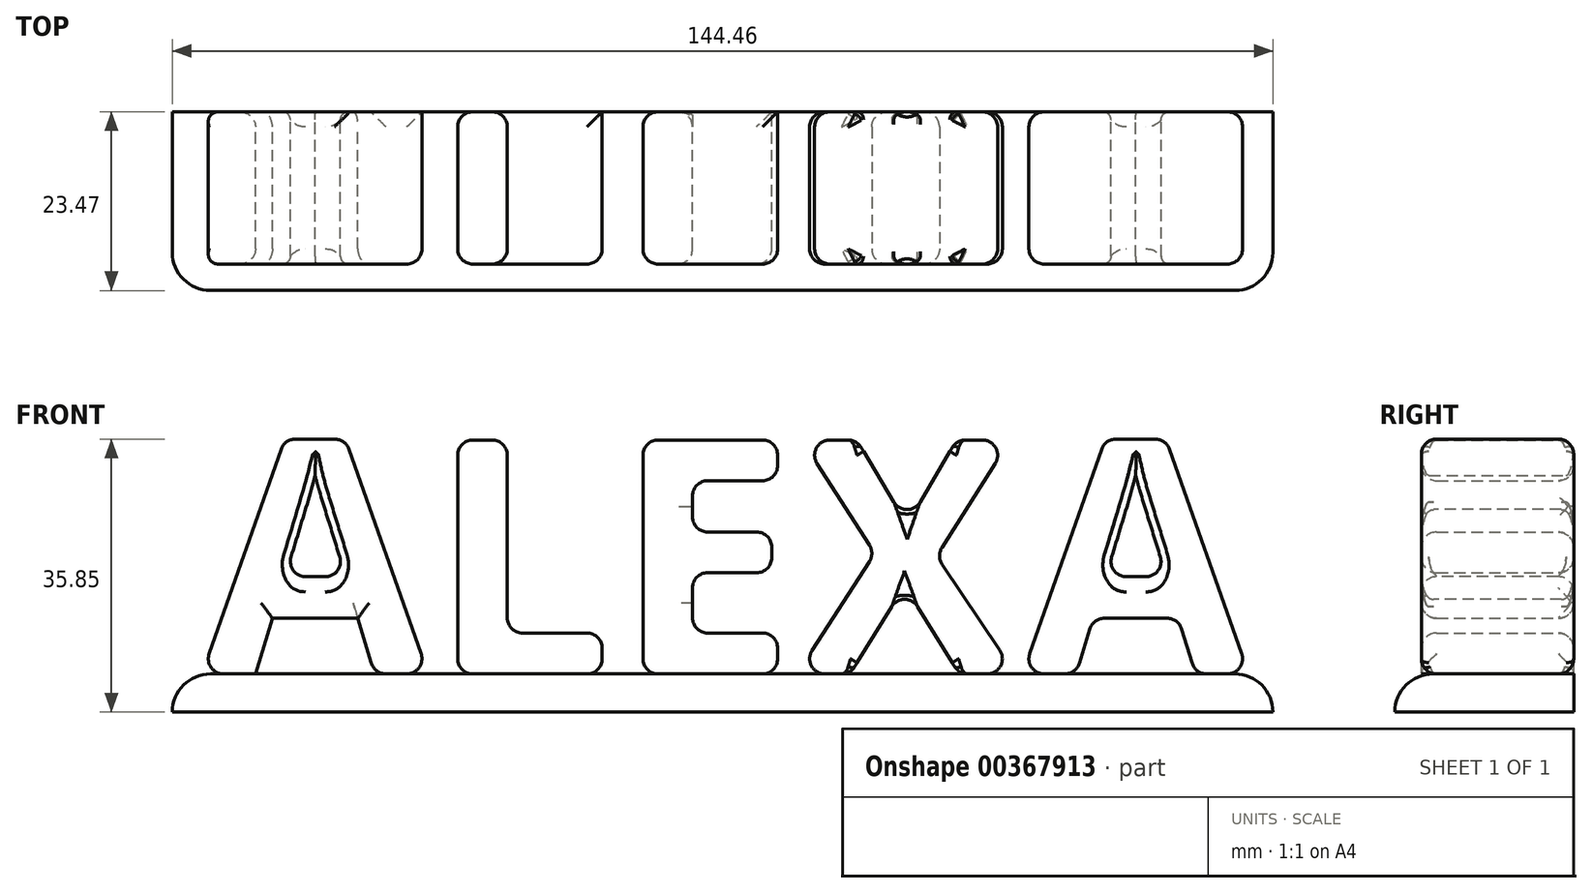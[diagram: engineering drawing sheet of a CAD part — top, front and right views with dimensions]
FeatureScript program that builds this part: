
annotation { "Feature Type Name" : "Feature", "Feature Type Description" : "" }
export const myFeature = defineFeature(function(context is Context, id is Id, definition is map)
    precondition{}
    {
        {
            var Q0;
            Q0=qCreatedBy(makeId("Front.planeOp"),FACE);
            var sketch = newSketch(context, id + "F0", { "sketchPlane" : qUnion([Q0])});
            skText(sketch, "E0", { "text": "ALEXA", "fontName": "OpenSans-Bold.ttf"});
            const initialGuessF0  = {"E0": [-0.06964, 0, 1, 0, 0.03098]};
            skSetInitialGuess(sketch, initialGuessF0);
            skSolve(sketch);
        }
        {
            var Q0;
            Q0 = qSketchRegion(id + "F0", true);
            extrude(context, id + "F1", {"entities" : qUnion([Q0]), "depth" : 20 * mm});
        }
        {
            var Q0;
            Q0=makeQuery(id+"F1.opExtrude","CAP_EDGE",EDGE,{"disambiguationData":[OSD([sQuery(id+"F0.wireOp",EDGE,"E0.sketch_text.stroke-8")])],"isStart":false});
            var Q1;
            Q1=makeQuery(id+"F1.opExtrude","CAP_EDGE",EDGE,{"disambiguationData":[OSD([sQuery(id+"F0.wireOp",EDGE,"E0.sketch_text.stroke-10")])],"isStart":false});
            var Q2;
            Q2=makeQuery(id+"F1.opExtrude","CAP_EDGE",EDGE,{"disambiguationData":[OSD([sQuery(id+"F0.wireOp",EDGE,"E0.sketch_text.stroke-37")])],"isStart":false});
            var Q3;
            Q3=makeQuery(id+"F1.opExtrude","CAP_EDGE",EDGE,{"disambiguationData":[OSD([sQuery(id+"F0.wireOp",EDGE,"E0.sketch_text.stroke-38")])],"isStart":false});
            var Q4;
            Q4=makeQuery(id+"F1.opExtrude","CAP_EDGE",EDGE,{"disambiguationData":[OSD([sQuery(id+"F0.wireOp",EDGE,"E0.sketch_text.stroke-31")])],"isStart":false});
            var Q5;
            Q5=makeQuery(id+"F1.opExtrude","CAP_EDGE",EDGE,{"disambiguationData":[OSD([sQuery(id+"F0.wireOp",EDGE,"E0.sketch_text.stroke-32")])],"isStart":false});
            var Q6;
            Q6=makeQuery(id+"F1.opExtrude","CAP_EDGE",EDGE,{"disambiguationData":[OSD([sQuery(id+"F0.wireOp",EDGE,"E0.sketch_text.stroke-50")])],"isStart":false});
            var Q7;
            Q7=makeQuery(id+"F1.opExtrude","CAP_EDGE",EDGE,{"disambiguationData":[OSD([sQuery(id+"F0.wireOp",EDGE,"E0.sketch_text.stroke-52")])],"isStart":false});
            var Q8;
            Q8=makeQuery(id+"F1.opExtrude","CAP_EDGE",EDGE,{"disambiguationData":[OSD([sQuery(id+"F0.wireOp",EDGE,"E0.sketch_text.stroke-52")])],"isStart":true});
            var Q9;
            Q9=makeQuery(id+"F1.opExtrude","CAP_EDGE",EDGE,{"disambiguationData":[OSD([sQuery(id+"F0.wireOp",EDGE,"E0.sketch_text.stroke-50")])],"isStart":true});
            var Q10;
            Q10=makeQuery(id+"F1.opExtrude","CAP_EDGE",EDGE,{"disambiguationData":[OSD([sQuery(id+"F0.wireOp",EDGE,"E0.sketch_text.stroke-38")])],"isStart":true});
            var Q11;
            Q11=makeQuery(id+"F1.opExtrude","CAP_EDGE",EDGE,{"disambiguationData":[OSD([sQuery(id+"F0.wireOp",EDGE,"E0.sketch_text.stroke-37")])],"isStart":true});
            var Q12;
            Q12=makeQuery(id+"F1.opExtrude","CAP_EDGE",EDGE,{"disambiguationData":[OSD([sQuery(id+"F0.wireOp",EDGE,"E0.sketch_text.stroke-32")])],"isStart":true});
            var Q13;
            Q13=makeQuery(id+"F1.opExtrude","CAP_EDGE",EDGE,{"disambiguationData":[OSD([sQuery(id+"F0.wireOp",EDGE,"E0.sketch_text.stroke-31")])],"isStart":true});
            var Q14;
            Q14=makeQuery(id+"F1.opExtrude","CAP_EDGE",EDGE,{"disambiguationData":[OSD([sQuery(id+"F0.wireOp",EDGE,"E0.sketch_text.stroke-8")])],"isStart":true});
            var Q15;
            Q15=makeQuery(id+"F1.opExtrude","CAP_EDGE",EDGE,{"disambiguationData":[OSD([sQuery(id+"F0.wireOp",EDGE,"E0.sketch_text.stroke-10")])],"isStart":true});
            fillet(context, id + "F2", {"entities" : qUnion([Q0, Q1, Q2, Q3, Q4, Q5, Q6, Q7, Q8, Q9, Q10, Q11, Q12, Q13, Q14, Q15]), "radius" : 1 * mm, "tangentPropagation" : true, "allowEdgeOverflow" : false});
        }
        {
            var Q0;
            Q0=makeQuery(id+"F1.opExtrude","CAP_EDGE",EDGE,{"disambiguationData":[OSD([sQuery(id+"F0.wireOp",EDGE,"E0.sketch_text.stroke-5")])],"isStart":false});
            var Q1;
            Q1=makeQuery(id+"F1.opExtrude","CAP_EDGE",EDGE,{"disambiguationData":[OSD([sQuery(id+"F0.wireOp",EDGE,"E0.sketch_text.stroke-4")])],"isStart":false});
            var Q2;
            Q2=makeQuery(id+"F1.opExtrude","CAP_EDGE",EDGE,{"disambiguationData":[OSD([sQuery(id+"F0.wireOp",EDGE,"E0.sketch_text.stroke-6")])],"isStart":false});
            var Q3;
            Q3=makeQuery(id+"F1.opExtrude","CAP_EDGE",EDGE,{"disambiguationData":[OSD([sQuery(id+"F0.wireOp",EDGE,"E0.sketch_text.stroke-11")])],"isStart":false});
            var Q4;
            Q4=makeQuery(id+"F1.opExtrude","CAP_EDGE",EDGE,{"disambiguationData":[OSD([sQuery(id+"F0.wireOp",EDGE,"E0.sketch_text.stroke-0")])],"isStart":false});
            var Q5;
            Q5=makeQuery(id+"F1.opExtrude","CAP_EDGE",EDGE,{"disambiguationData":[OSD([sQuery(id+"F0.wireOp",EDGE,"E0.sketch_text.stroke-2")])],"isStart":false});
            var Q6;
            Q6=makeQuery(id+"F1.opExtrude","CAP_EDGE",EDGE,{"disambiguationData":[OSD([sQuery(id+"F0.wireOp",EDGE,"E0.sketch_text.stroke-1")])],"isStart":false});
            var Q7;
            Q7=makeQuery(id+"F1.opExtrude","CAP_EDGE",EDGE,{"disambiguationData":[OSD([sQuery(id+"F0.wireOp",EDGE,"E0.sketch_text.stroke-7")])],"isStart":false});
            var Q8;
            Q8=makeQuery(id+"F1.opExtrude","SWEPT_EDGE",EDGE,{"disambiguationData":[OSD([sQuery(id+"F0.wireOp",EDGE,"E0.sketch_text.stroke-0"),sQuery(id+"F0.wireOp",EDGE,"E0.sketch_text.stroke-7")])]});
            var Q9;
            Q9=makeQuery(id+"F1.opExtrude","CAP_EDGE",EDGE,{"disambiguationData":[OSD([sQuery(id+"F0.wireOp",EDGE,"E0.sketch_text.stroke-7")])],"isStart":true});
            var Q10;
            Q10=makeQuery(id+"F1.opExtrude","SWEPT_EDGE",EDGE,{"disambiguationData":[OSD([sQuery(id+"F0.wireOp",EDGE,"E0.sketch_text.stroke-6"),sQuery(id+"F0.wireOp",EDGE,"E0.sketch_text.stroke-7")])]});
            var Q11;
            Q11=makeQuery(id+"F1.opExtrude","SWEPT_EDGE",EDGE,{"disambiguationData":[OSD([sQuery(id+"F0.wireOp",EDGE,"E0.sketch_text.stroke-5"),sQuery(id+"F0.wireOp",EDGE,"E0.sketch_text.stroke-6")])]});
            var Q12;
            Q12=makeQuery(id+"F1.opExtrude","SWEPT_EDGE",EDGE,{"disambiguationData":[OSD([sQuery(id+"F0.wireOp",EDGE,"E0.sketch_text.stroke-4"),sQuery(id+"F0.wireOp",EDGE,"E0.sketch_text.stroke-5")])]});
            var Q13;
            Q13=makeQuery(id+"F1.opExtrude","CAP_EDGE",EDGE,{"disambiguationData":[OSD([sQuery(id+"F0.wireOp",EDGE,"E0.sketch_text.stroke-4")])],"isStart":true});
            var Q14;
            Q14=makeQuery(id+"F1.opExtrude","SWEPT_EDGE",EDGE,{"disambiguationData":[OSD([sQuery(id+"F0.wireOp",EDGE,"E0.sketch_text.stroke-3"),sQuery(id+"F0.wireOp",EDGE,"E0.sketch_text.stroke-4")])]});
            var Q15;
            Q15=makeQuery(id+"F1.opExtrude","CAP_EDGE",EDGE,{"disambiguationData":[OSD([sQuery(id+"F0.wireOp",EDGE,"E0.sketch_text.stroke-2")])],"isStart":true});
            var Q16;
            Q16=makeQuery(id+"F1.opExtrude","CAP_EDGE",EDGE,{"disambiguationData":[OSD([sQuery(id+"F0.wireOp",EDGE,"E0.sketch_text.stroke-1")])],"isStart":true});
            var Q17;
            Q17=makeQuery(id+"F1.opExtrude","CAP_EDGE",EDGE,{"disambiguationData":[OSD([sQuery(id+"F0.wireOp",EDGE,"E0.sketch_text.stroke-5")])],"isStart":true});
            var Q18;
            Q18=makeQuery(id+"F1.opExtrude","SWEPT_FACE",FACE,{"disambiguationData":[OSD([sQuery(id+"F0.wireOp",EDGE,"E0.sketch_text.stroke-13")])]});
            var Q19;
            Q19=makeQuery(id+"F1.opExtrude","SWEPT_FACE",FACE,{"disambiguationData":[OSD([sQuery(id+"F0.wireOp",EDGE,"E0.sketch_text.stroke-12")])]});
            var Q20;
            Q20=makeQuery(id+"F1.opExtrude","SWEPT_FACE",FACE,{"disambiguationData":[OSD([sQuery(id+"F0.wireOp",EDGE,"E0.sketch_text.stroke-15")])]});
            var Q21;
            Q21=makeQuery(id+"F1.opExtrude","SWEPT_FACE",FACE,{"disambiguationData":[OSD([sQuery(id+"F0.wireOp",EDGE,"E0.sketch_text.stroke-14")])]});
            var Q22;
            Q22=makeQuery(id+"F1.opExtrude","CAP_FACE",FACE,{"disambiguationData":[OSD([sQuery(id+"F0.wireOp",EDGE,"E0.sketch_text.stroke-12"),sQuery(id+"F0.wireOp",EDGE,"E0.sketch_text.stroke-13"),sQuery(id+"F0.wireOp",EDGE,"E0.sketch_text.stroke-14"),sQuery(id+"F0.wireOp",EDGE,"E0.sketch_text.stroke-15"),sQuery(id+"F0.wireOp",EDGE,"E0.sketch_text.stroke-16"),sQuery(id+"F0.wireOp",EDGE,"E0.sketch_text.stroke-17")])],"isStart":false});
            var Q23;
            Q23=makeQuery(id+"F1.opExtrude","CAP_FACE",FACE,{"disambiguationData":[OSD([sQuery(id+"F0.wireOp",EDGE,"E0.sketch_text.stroke-18"),sQuery(id+"F0.wireOp",EDGE,"E0.sketch_text.stroke-19"),sQuery(id+"F0.wireOp",EDGE,"E0.sketch_text.stroke-20"),sQuery(id+"F0.wireOp",EDGE,"E0.sketch_text.stroke-21"),sQuery(id+"F0.wireOp",EDGE,"E0.sketch_text.stroke-22"),sQuery(id+"F0.wireOp",EDGE,"E0.sketch_text.stroke-23"),sQuery(id+"F0.wireOp",EDGE,"E0.sketch_text.stroke-24"),sQuery(id+"F0.wireOp",EDGE,"E0.sketch_text.stroke-25"),sQuery(id+"F0.wireOp",EDGE,"E0.sketch_text.stroke-26"),sQuery(id+"F0.wireOp",EDGE,"E0.sketch_text.stroke-27"),sQuery(id+"F0.wireOp",EDGE,"E0.sketch_text.stroke-28"),sQuery(id+"F0.wireOp",EDGE,"E0.sketch_text.stroke-29")])],"isStart":false});
            var Q24;
            Q24=makeQuery(id+"F1.opExtrude","SWEPT_FACE",FACE,{"disambiguationData":[OSD([sQuery(id+"F0.wireOp",EDGE,"E0.sketch_text.stroke-20")])]});
            var Q25;
            Q25=makeQuery(id+"F1.opExtrude","SWEPT_FACE",FACE,{"disambiguationData":[OSD([sQuery(id+"F0.wireOp",EDGE,"E0.sketch_text.stroke-19")])]});
            var Q26;
            Q26=makeQuery(id+"F1.opExtrude","SWEPT_FACE",FACE,{"disambiguationData":[OSD([sQuery(id+"F0.wireOp",EDGE,"E0.sketch_text.stroke-22")])]});
            var Q27;
            Q27=makeQuery(id+"F1.opExtrude","SWEPT_FACE",FACE,{"disambiguationData":[OSD([sQuery(id+"F0.wireOp",EDGE,"E0.sketch_text.stroke-26")])]});
            var Q28;
            Q28=makeQuery(id+"F1.opExtrude","SWEPT_FACE",FACE,{"disambiguationData":[OSD([sQuery(id+"F0.wireOp",EDGE,"E0.sketch_text.stroke-18")])]});
            var Q29;
            Q29=makeQuery(id+"F1.opExtrude","SWEPT_FACE",FACE,{"disambiguationData":[OSD([sQuery(id+"F0.wireOp",EDGE,"E0.sketch_text.stroke-28")])]});
            var Q30;
            Q30=makeQuery(id+"F1.opExtrude","SWEPT_FACE",FACE,{"disambiguationData":[OSD([sQuery(id+"F0.wireOp",EDGE,"E0.sketch_text.stroke-24")])]});
            var Q31;
            Q31=makeQuery(id+"F1.opExtrude","CAP_FACE",FACE,{"disambiguationData":[OSD([sQuery(id+"F0.wireOp",EDGE,"E0.sketch_text.stroke-30"),sQuery(id+"F0.wireOp",EDGE,"E0.sketch_text.stroke-31"),sQuery(id+"F0.wireOp",EDGE,"E0.sketch_text.stroke-32"),sQuery(id+"F0.wireOp",EDGE,"E0.sketch_text.stroke-33"),sQuery(id+"F0.wireOp",EDGE,"E0.sketch_text.stroke-34"),sQuery(id+"F0.wireOp",EDGE,"E0.sketch_text.stroke-35"),sQuery(id+"F0.wireOp",EDGE,"E0.sketch_text.stroke-36"),sQuery(id+"F0.wireOp",EDGE,"E0.sketch_text.stroke-37"),sQuery(id+"F0.wireOp",EDGE,"E0.sketch_text.stroke-38"),sQuery(id+"F0.wireOp",EDGE,"E0.sketch_text.stroke-39"),sQuery(id+"F0.wireOp",EDGE,"E0.sketch_text.stroke-40"),sQuery(id+"F0.wireOp",EDGE,"E0.sketch_text.stroke-41")])],"isStart":false});
            var Q32;
            Q32=makeQuery(id+"F1.opExtrude","CAP_FACE",FACE,{"disambiguationData":[OSD([sQuery(id+"F0.wireOp",EDGE,"E0.sketch_text.stroke-30"),sQuery(id+"F0.wireOp",EDGE,"E0.sketch_text.stroke-31"),sQuery(id+"F0.wireOp",EDGE,"E0.sketch_text.stroke-32"),sQuery(id+"F0.wireOp",EDGE,"E0.sketch_text.stroke-33"),sQuery(id+"F0.wireOp",EDGE,"E0.sketch_text.stroke-34"),sQuery(id+"F0.wireOp",EDGE,"E0.sketch_text.stroke-35"),sQuery(id+"F0.wireOp",EDGE,"E0.sketch_text.stroke-36"),sQuery(id+"F0.wireOp",EDGE,"E0.sketch_text.stroke-37"),sQuery(id+"F0.wireOp",EDGE,"E0.sketch_text.stroke-38"),sQuery(id+"F0.wireOp",EDGE,"E0.sketch_text.stroke-39"),sQuery(id+"F0.wireOp",EDGE,"E0.sketch_text.stroke-40"),sQuery(id+"F0.wireOp",EDGE,"E0.sketch_text.stroke-41")])],"isStart":true});
            var Q33;
            Q33=makeQuery(id+"F1.opExtrude","SWEPT_FACE",FACE,{"disambiguationData":[OSD([sQuery(id+"F0.wireOp",EDGE,"E0.sketch_text.stroke-39")])]});
            var Q34;
            Q34=makeQuery(id+"F1.opExtrude","SWEPT_FACE",FACE,{"disambiguationData":[OSD([sQuery(id+"F0.wireOp",EDGE,"E0.sketch_text.stroke-36")])]});
            var Q35;
            Q35=makeQuery(id+"F1.opExtrude","SWEPT_FACE",FACE,{"disambiguationData":[OSD([sQuery(id+"F0.wireOp",EDGE,"E0.sketch_text.stroke-38")])]});
            var Q36;
            Q36=makeQuery(id+"F1.opExtrude","SWEPT_FACE",FACE,{"disambiguationData":[OSD([sQuery(id+"F0.wireOp",EDGE,"E0.sketch_text.stroke-37")])]});
            var Q37;
            Q37=makeQuery(id+"F1.opExtrude","SWEPT_FACE",FACE,{"disambiguationData":[OSD([sQuery(id+"F0.wireOp",EDGE,"E0.sketch_text.stroke-35")])]});
            var Q38;
            Q38=makeQuery(id+"F1.opExtrude","SWEPT_FACE",FACE,{"disambiguationData":[OSD([sQuery(id+"F0.wireOp",EDGE,"E0.sketch_text.stroke-31")])]});
            var Q39;
            Q39=makeQuery(id+"F1.opExtrude","SWEPT_FACE",FACE,{"disambiguationData":[OSD([sQuery(id+"F0.wireOp",EDGE,"E0.sketch_text.stroke-34")])]});
            var Q40;
            Q40=makeQuery(id+"F1.opExtrude","SWEPT_FACE",FACE,{"disambiguationData":[OSD([sQuery(id+"F0.wireOp",EDGE,"E0.sketch_text.stroke-41")])]});
            var Q41;
            Q41=makeQuery(id+"F1.opExtrude","SWEPT_FACE",FACE,{"disambiguationData":[OSD([sQuery(id+"F0.wireOp",EDGE,"E0.sketch_text.stroke-40")])]});
            var Q42;
            Q42=makeQuery(id+"F1.opExtrude","CAP_FACE",FACE,{"disambiguationData":[OSD([sQuery(id+"F0.wireOp",EDGE,"E0.sketch_text.stroke-42"),sQuery(id+"F0.wireOp",EDGE,"E0.sketch_text.stroke-43"),sQuery(id+"F0.wireOp",EDGE,"E0.sketch_text.stroke-44"),sQuery(id+"F0.wireOp",EDGE,"E0.sketch_text.stroke-45"),sQuery(id+"F0.wireOp",EDGE,"E0.sketch_text.stroke-46"),sQuery(id+"F0.wireOp",EDGE,"E0.sketch_text.stroke-47"),sQuery(id+"F0.wireOp",EDGE,"E0.sketch_text.stroke-48"),sQuery(id+"F0.wireOp",EDGE,"E0.sketch_text.stroke-49"),sQuery(id+"F0.wireOp",EDGE,"E0.sketch_text.stroke-50"),sQuery(id+"F0.wireOp",EDGE,"E0.sketch_text.stroke-51"),sQuery(id+"F0.wireOp",EDGE,"E0.sketch_text.stroke-52"),sQuery(id+"F0.wireOp",EDGE,"E0.sketch_text.stroke-53")])],"isStart":false});
            var Q43;
            Q43=makeQuery(id+"F1.opExtrude","SWEPT_FACE",FACE,{"disambiguationData":[OSD([sQuery(id+"F0.wireOp",EDGE,"E0.sketch_text.stroke-48")])]});
            var Q44;
            Q44=makeQuery(id+"F1.opExtrude","SWEPT_EDGE",EDGE,{"disambiguationData":[OSD([sQuery(id+"F0.wireOp",EDGE,"E0.sketch_text.stroke-46"),sQuery(id+"F0.wireOp",EDGE,"E0.sketch_text.stroke-47")])]});
            var Q45;
            Q45=makeQuery(id+"F1.opExtrude","CAP_FACE",FACE,{"disambiguationData":[OSD([sQuery(id+"F0.wireOp",EDGE,"E0.sketch_text.stroke-42"),sQuery(id+"F0.wireOp",EDGE,"E0.sketch_text.stroke-43"),sQuery(id+"F0.wireOp",EDGE,"E0.sketch_text.stroke-44"),sQuery(id+"F0.wireOp",EDGE,"E0.sketch_text.stroke-45"),sQuery(id+"F0.wireOp",EDGE,"E0.sketch_text.stroke-46"),sQuery(id+"F0.wireOp",EDGE,"E0.sketch_text.stroke-47"),sQuery(id+"F0.wireOp",EDGE,"E0.sketch_text.stroke-48"),sQuery(id+"F0.wireOp",EDGE,"E0.sketch_text.stroke-49"),sQuery(id+"F0.wireOp",EDGE,"E0.sketch_text.stroke-50"),sQuery(id+"F0.wireOp",EDGE,"E0.sketch_text.stroke-51"),sQuery(id+"F0.wireOp",EDGE,"E0.sketch_text.stroke-52"),sQuery(id+"F0.wireOp",EDGE,"E0.sketch_text.stroke-53")])],"isStart":true});
            var Q46;
            Q46=makeQuery(id+"F1.opExtrude","SWEPT_FACE",FACE,{"disambiguationData":[OSD([sQuery(id+"F0.wireOp",EDGE,"E0.sketch_text.stroke-49")])]});
            var Q47;
            Q47=makeQuery(id+"F1.opExtrude","SWEPT_FACE",FACE,{"disambiguationData":[OSD([sQuery(id+"F0.wireOp",EDGE,"E0.sketch_text.stroke-45")])]});
            var Q48;
            Q48=makeQuery(id+"F1.opExtrude","SWEPT_FACE",FACE,{"disambiguationData":[OSD([sQuery(id+"F0.wireOp",EDGE,"E0.sketch_text.stroke-43")])]});
            var Q49;
            Q49=makeQuery(id+"F1.opExtrude","SWEPT_FACE",FACE,{"disambiguationData":[OSD([sQuery(id+"F0.wireOp",EDGE,"E0.sketch_text.stroke-53")])]});
            var Q50;
            Q50=makeQuery(id+"F1.opExtrude","SWEPT_FACE",FACE,{"disambiguationData":[OSD([sQuery(id+"F0.wireOp",EDGE,"E0.sketch_text.stroke-11")])]});
            var Q51;
            Q51=makeQuery(id+"F1.opExtrude","SWEPT_FACE",FACE,{"disambiguationData":[OSD([sQuery(id+"F0.wireOp",EDGE,"E0.sketch_text.stroke-17")])]});
            fillet(context, id + "F3", {"entities" : qUnion([Q0, Q1, Q2, Q3, Q4, Q5, Q6, Q7, Q8, Q9, Q10, Q11, Q12, Q13, Q14, Q15, Q16, Q17, Q18, Q19, Q20, Q21, Q22, Q23, Q24, Q25, Q26, Q27, Q28, Q29, Q30, Q31, Q32, Q33, Q34, Q35, Q36, Q37, Q38, Q39, Q40, Q41, Q42, Q43, Q44, Q45, Q46, Q47, Q48, Q49, Q50, Q51]), "radius" : 2 * mm, "tangentPropagation" : true, "allowEdgeOverflow" : false});
        }
        {
            var Q0;
            Q0=makeQuery(id+"F1.opExtrude","SWEPT_FACE",FACE,{"disambiguationData":[OSD([sQuery(id+"F0.wireOp",EDGE,"E0.sketch_text.stroke-18")])]});
            var sketch = newSketch(context, id + "F4", { "sketchPlane" : qUnion([Q0])});
            skLineSegment(sketch, "E1.bottom", {"start": v(-73.53, 23.47) * mm, "end": v(70.93, 23.47) * mm});
            skLineSegment(sketch, "E1.top", {"start": v(-73.53, 0) * mm, "end": v(70.93, 0) * mm});
            skLineSegment(sketch, "E1.left", {"start": v(-73.53, 23.47) * mm, "end": v(-73.53, 0) * mm});
            skLineSegment(sketch, "E1.right", {"start": v(70.93, 23.47) * mm, "end": v(70.93, 0) * mm});
            skSolve(sketch);
        }
        {
            var Q0;
            Q0 = qSketchRegion(id + "F4", true);
            extrude(context, id + "F5", {"entities" : qUnion([Q0]), "depth" : 5 * mm});
        }
        {
            var Q0;
            Q0=makeQuery(id+"F5.opExtrude","CAP_EDGE",EDGE,{"disambiguationData":[OSD([sQuery(id+"F4.wireOp",EDGE,"E1.bottom")])],"isStart":true});
            var Q1;
            Q1=makeQuery(id+"F5.opExtrude","CAP_EDGE",EDGE,{"disambiguationData":[OSD([sQuery(id+"F4.wireOp",EDGE,"E1.left")])],"isStart":true});
            var Q2;
            Q2=makeQuery(id+"F5.opExtrude","SWEPT_EDGE",EDGE,{"disambiguationData":[OSD([sQuery(id+"F4.wireOp",EDGE,"E1.bottom"),sQuery(id+"F4.wireOp",EDGE,"E1.left")])]});
            var Q3;
            Q3=makeQuery(id+"F5.opExtrude","CAP_EDGE",EDGE,{"disambiguationData":[OSD([sQuery(id+"F4.wireOp",EDGE,"E1.right")])],"isStart":true});
            var Q4;
            Q4=makeQuery(id+"F5.opExtrude","SWEPT_EDGE",EDGE,{"disambiguationData":[OSD([sQuery(id+"F4.wireOp",EDGE,"E1.bottom"),sQuery(id+"F4.wireOp",EDGE,"E1.right")])]});
            fillet(context, id + "F6", {"entities" : qUnion([Q0, Q1, Q2, Q3, Q4]), "radius" : 5 * mm, "tangentPropagation" : true, "allowEdgeOverflow" : false});
        }
    });
